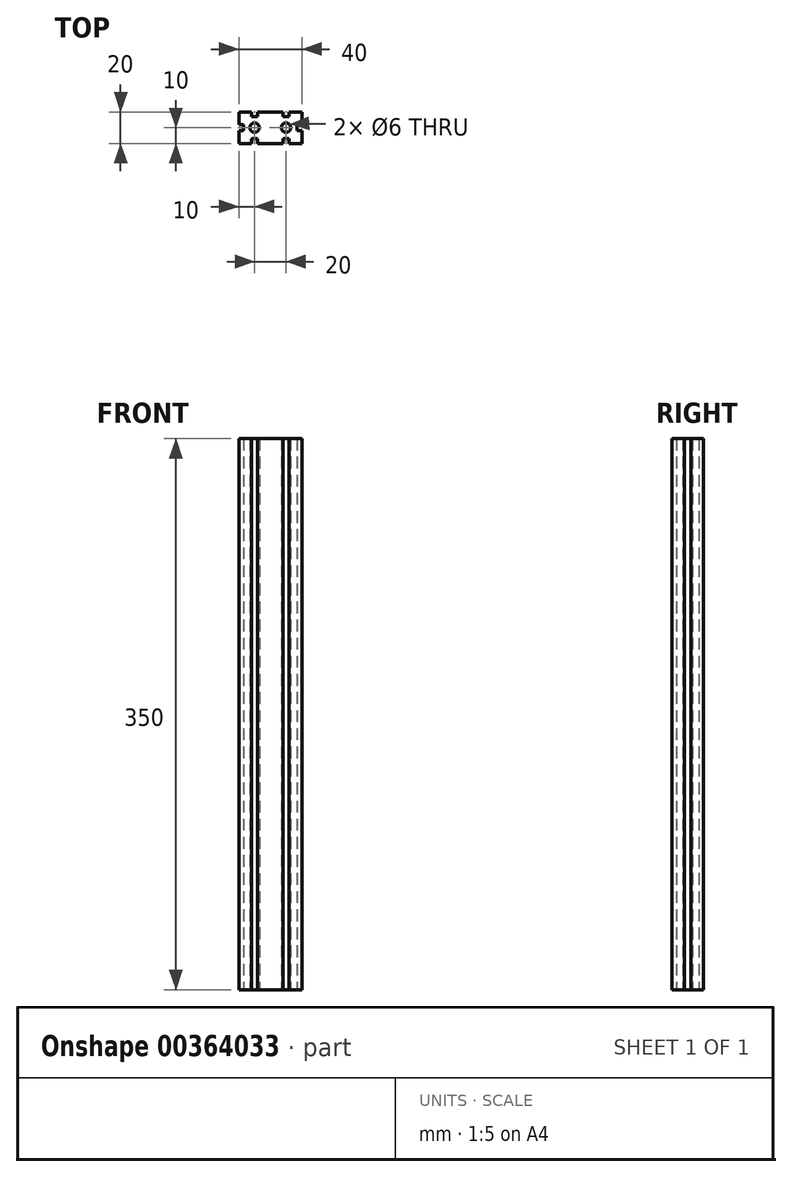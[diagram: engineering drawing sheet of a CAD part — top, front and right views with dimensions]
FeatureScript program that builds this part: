
annotation { "Feature Type Name" : "Feature", "Feature Type Description" : "" }
export const myFeature = defineFeature(function(context is Context, id is Id, definition is map)
    precondition{}
    {
        {
            var Q0;
            Q0=qCreatedBy(makeId("Top.planeOp"),FACE);
            var sketch = newSketch(context, id + "F0", { "sketchPlane" : qUnion([Q0])});
            skPoint(sketch, "E0.middle", {"position": v(0, 0) * mm});
            skLineSegment(sketch, "E1", {"start": v(-20, 10) * mm, "end": v(-12, 10) * mm});
            skLineSegment(sketch, "E2", {"start": v(-12, 10) * mm, "end": v(-12, 7) * mm});
            skLineSegment(sketch, "E3", {"start": v(-12, 7) * mm, "end": v(-8, 7) * mm});
            skLineSegment(sketch, "E4", {"start": v(-8, 7) * mm, "end": v(-8, 10) * mm});
            skLineSegment(sketch, "E5", {"start": v(-8, 10) * mm, "end": v(8, 10) * mm});
            skLineSegment(sketch, "E6", {"start": v(8, 10) * mm, "end": v(8, 7) * mm});
            skLineSegment(sketch, "E7", {"start": v(8, 7) * mm, "end": v(12, 7) * mm});
            skLineSegment(sketch, "E8", {"start": v(12, 7) * mm, "end": v(12, 10) * mm});
            skLineSegment(sketch, "E9", {"start": v(12, 10) * mm, "end": v(20, 10) * mm});
            skLineSegment(sketch, "E10", {"start": v(20, 2) * mm, "end": v(17, 2) * mm});
            skLineSegment(sketch, "E11", {"start": v(17, 2) * mm, "end": v(17, -2) * mm});
            skLineSegment(sketch, "E12", {"start": v(17, -2) * mm, "end": v(20, -2) * mm});
            skLineSegment(sketch, "E13", {"start": v(20, -2) * mm, "end": v(20, -10) * mm});
            skLineSegment(sketch, "E14", {"start": v(12, -10) * mm, "end": v(12, -7) * mm});
            skLineSegment(sketch, "E15", {"start": v(12, -7) * mm, "end": v(8, -7) * mm});
            skLineSegment(sketch, "E16", {"start": v(8, -7) * mm, "end": v(8, -10) * mm});
            skLineSegment(sketch, "E17", {"start": v(8, -10) * mm, "end": v(-8, -10) * mm});
            skLineSegment(sketch, "E18", {"start": v(-8, -10) * mm, "end": v(-8, -7) * mm});
            skLineSegment(sketch, "E19", {"start": v(-8, -7) * mm, "end": v(-12, -7) * mm});
            skLineSegment(sketch, "E20", {"start": v(-12, -7) * mm, "end": v(-12, -10) * mm});
            skLineSegment(sketch, "E21", {"start": v(-12, -10) * mm, "end": v(-20, -10) * mm});
            skLineSegment(sketch, "E22", {"start": v(-20, -2) * mm, "end": v(-17, -2) * mm});
            skLineSegment(sketch, "E23", {"start": v(-17, -2) * mm, "end": v(-17, 2) * mm});
            skLineSegment(sketch, "E24", {"start": v(-17, 2) * mm, "end": v(-20, 2) * mm});
            skLineSegment(sketch, "E25", {"start": v(-20, 2) * mm, "end": v(-20, 10) * mm});
            skLineSegment(sketch, "E26", {"start": v(-20, -2) * mm, "end": v(-20, -10) * mm});
            skLineSegment(sketch, "E27", {"start": v(20, 10) * mm, "end": v(20, 2) * mm});
            skLineSegment(sketch, "E28", {"start": v(20, -10) * mm, "end": v(12, -10) * mm});
            skLineSegment(sketch, "E29", {"start": v(0, 0) * mm, "end": v(-10, 0) * mm, "construction": true});
            skLineSegment(sketch, "E30", {"start": v(0, 0) * mm, "end": v(10, 0) * mm, "construction": true});
            skCircle(sketch, "E31", {"center": v(-10, 0) * mm, "radius": 3 * mm});
            skCircle(sketch, "E32", {"center": v(10, 0) * mm, "radius": 3 * mm});
            skSolve(sketch);
        }
        {
            var Q0;
            Q0 = qSketchRegion(id + "F0", true);
            extrude(context, id + "F1", {"entities" : qUnion([Q0]), "depth" : 350 * mm});
        }
    });
